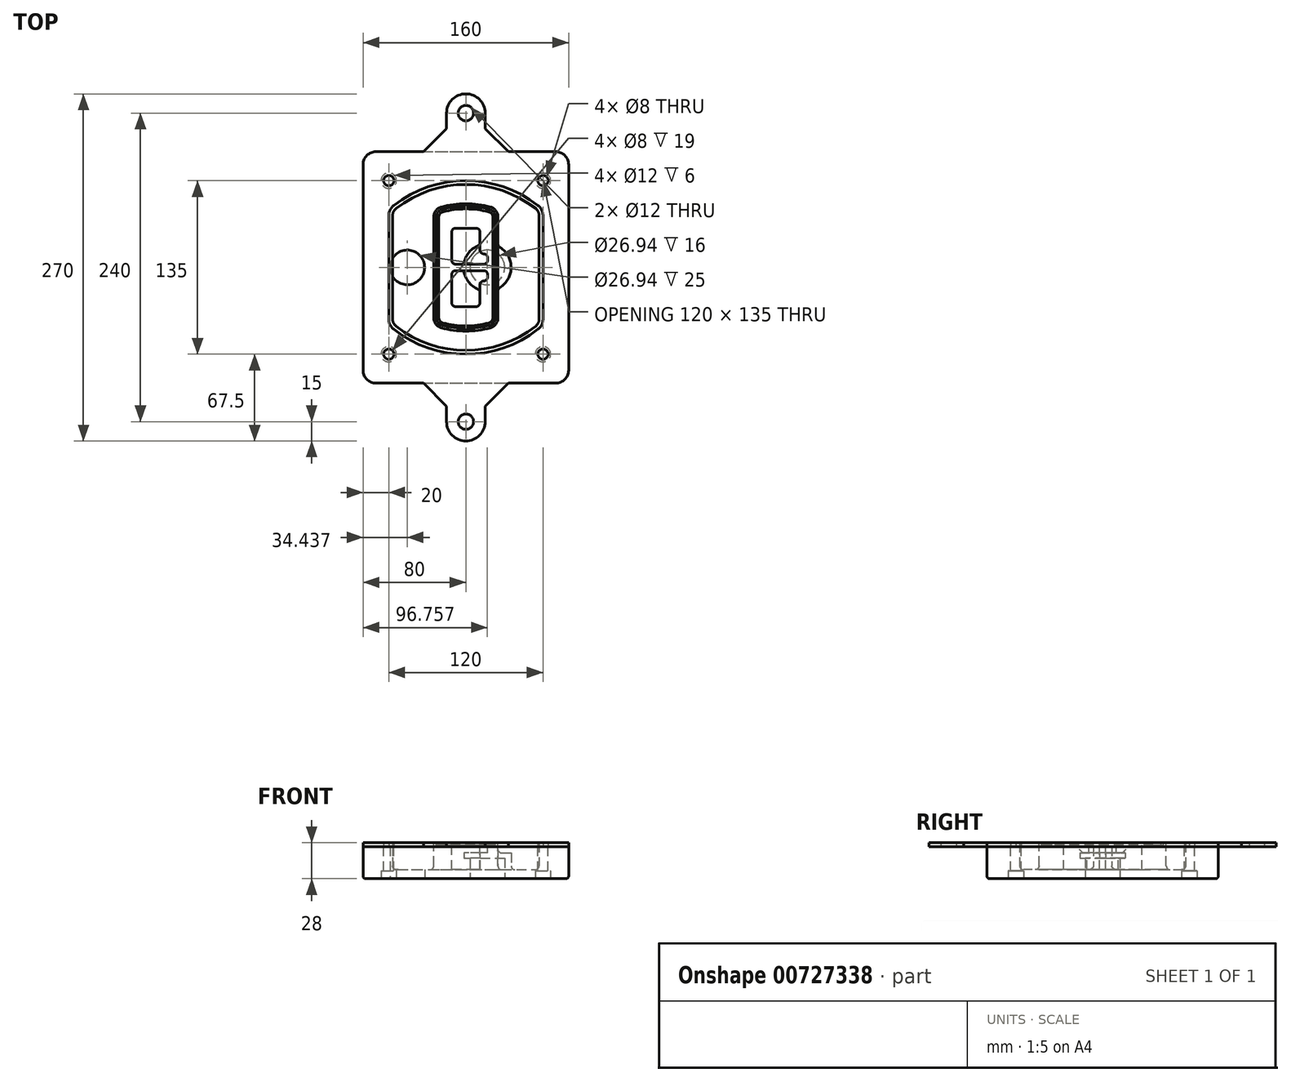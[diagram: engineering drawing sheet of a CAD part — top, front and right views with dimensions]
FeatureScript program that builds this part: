
annotation { "Feature Type Name" : "Feature", "Feature Type Description" : "" }
export const myFeature = defineFeature(function(context is Context, id is Id, definition is map)
    precondition{}
    {
        {
            var Q0;
            Q0=qCreatedBy(makeId("Top.planeOp"),FACE);
            var sketch = newSketch(context, id + "F0", { "sketchPlane" : qUnion([Q0])});
            skPoint(sketch, "E0.rect.middle", {"position": v(0, 0) * mm});
            skLineSegment(sketch, "E1.bottom", {"start": v(-70, -90) * mm, "end": v(70, -90) * mm});
            skLineSegment(sketch, "E1.top", {"start": v(-70, 90) * mm, "end": v(70, 90) * mm});
            skLineSegment(sketch, "E1.left", {"start": v(-80, -80) * mm, "end": v(-80, 80) * mm});
            skLineSegment(sketch, "E1.right", {"start": v(80, -80) * mm, "end": v(80, 80) * mm});
            skLineSegment(sketch, "E2", {"start": v(-80, 90) * mm, "end": v(80, -90) * mm, "construction": true});
            skLineSegment(sketch, "E3", {"start": v(80, 90) * mm, "end": v(-80, -90) * mm, "construction": true});
            skCircle(sketch, "E4", {"center": v(-60, 67.5) * mm, "radius": 4 * mm});
            skCircle(sketch, "E5", {"center": v(60, 67.5) * mm, "radius": 4 * mm});
            skCircle(sketch, "E6", {"center": v(60, -67.5) * mm, "radius": 4 * mm});
            skCircle(sketch, "E7", {"center": v(-60, -67.5) * mm, "radius": 4 * mm});
            skLineSegment(sketch, "E8", {"start": v(-60, 67.5) * mm, "end": v(60, 67.5) * mm, "construction": true});
            skLineSegment(sketch, "E9", {"start": v(60, 67.5) * mm, "end": v(60, -67.5) * mm, "construction": true});
            skLineSegment(sketch, "E10", {"start": v(60, -67.5) * mm, "end": v(-60, -67.5) * mm, "construction": true});
            skLineSegment(sketch, "E11", {"start": v(-60, -67.5) * mm, "end": v(-60, 67.5) * mm, "construction": true});
            skLineSegment(sketch, "E12", {"start": v(-60, 40.3) * mm, "end": v(-60, -40.3) * mm});
            skLineSegment(sketch, "E13", {"start": v(60, 40.3) * mm, "end": v(60, -40.3) * mm});
            skArc(sketch, "E14", {"start": v(56.15, 48.18) * mm, "mid": v(0, 67.5) * mm, "end": v(-56.15, 48.18) * mm});
            skArc(sketch, "E15", {"start": v(-56.15, -48.18) * mm, "mid": v(0, -67.5) * mm, "end": v(56.15, -48.18) * mm});
            skLineSegment(sketch, "E16", {"start": v(-60, 0) * mm, "end": v(60, 0) * mm, "construction": true});
            skPoint(sketch, "E17.visualSharp", {"position": v(-60, -45) * mm});
            skArc(sketch, "E17.filletArc", {"start": v(-60, -40.3) * mm, "mid": v(-58.99, -44.68) * mm, "end": v(-56.15, -48.18) * mm});
            skPoint(sketch, "E18.visualSharp", {"position": v(-60, 45) * mm});
            skArc(sketch, "E18.filletArc", {"start": v(-56.15, 48.18) * mm, "mid": v(-58.99, 44.68) * mm, "end": v(-60, 40.3) * mm});
            skPoint(sketch, "E19.visualSharp", {"position": v(60, 45) * mm});
            skArc(sketch, "E19.filletArc", {"start": v(60, 40.3) * mm, "mid": v(58.99, 44.68) * mm, "end": v(56.15, 48.18) * mm});
            skPoint(sketch, "E20.visualSharp", {"position": v(60, -45) * mm});
            skArc(sketch, "E20.filletArc", {"start": v(56.15, -48.18) * mm, "mid": v(58.99, -44.68) * mm, "end": v(60, -40.3) * mm});
            skPoint(sketch, "E21.visualSharp", {"position": v(-80, 90) * mm});
            skArc(sketch, "E21.filletArc", {"start": v(-70, 90) * mm, "mid": v(-77.07, 87.07) * mm, "end": v(-80, 80) * mm});
            skPoint(sketch, "E22.visualSharp", {"position": v(80, 90) * mm});
            skArc(sketch, "E22.filletArc", {"start": v(80, 80) * mm, "mid": v(77.07, 87.07) * mm, "end": v(70, 90) * mm});
            skPoint(sketch, "E23.visualSharp", {"position": v(80, -90) * mm});
            skArc(sketch, "E23.filletArc", {"start": v(70, -90) * mm, "mid": v(77.07, -87.07) * mm, "end": v(80, -80) * mm});
            skPoint(sketch, "E24.visualSharp", {"position": v(-80, -90) * mm});
            skArc(sketch, "E24.filletArc", {"start": v(-80, -80) * mm, "mid": v(-77.07, -87.07) * mm, "end": v(-70, -90) * mm});
            skArc(sketch, "E25.0", {"start": v(57, 40.3) * mm, "mid": v(56.3, 43.36) * mm, "end": v(54.3, 45.81) * mm});
            skLineSegment(sketch, "E25.1", {"start": v(57, 40.3) * mm, "end": v(57, -40.3) * mm});
            skArc(sketch, "E25.2", {"start": v(54.3, -45.81) * mm, "mid": v(56.3, -43.36) * mm, "end": v(57, -40.3) * mm});
            skArc(sketch, "E25.3", {"start": v(-54.3, -45.81) * mm, "mid": v(0, -64.5) * mm, "end": v(54.3, -45.81) * mm});
            skArc(sketch, "E25.4", {"start": v(-57, -40.3) * mm, "mid": v(-56.3, -43.36) * mm, "end": v(-54.3, -45.81) * mm});
            skArc(sketch, "E25.5", {"start": v(54.3, 45.81) * mm, "mid": v(0, 64.5) * mm, "end": v(-54.3, 45.81) * mm});
            skLineSegment(sketch, "E25.6", {"start": v(-57, 40.3) * mm, "end": v(-57, -40.3) * mm});
            skArc(sketch, "E25.7", {"start": v(-54.3, 45.81) * mm, "mid": v(-56.3, 43.36) * mm, "end": v(-57, 40.3) * mm});
            skArc(sketch, "E26.0", {"start": v(-58.62, 51.33) * mm, "mid": v(-62.58, 46.43) * mm, "end": v(-64, 40.3) * mm});
            skArc(sketch, "E26.1", {"start": v(58.62, 51.33) * mm, "mid": v(0, 71.5) * mm, "end": v(-58.62, 51.33) * mm});
            skArc(sketch, "E26.2", {"start": v(64, 40.3) * mm, "mid": v(62.58, 46.43) * mm, "end": v(58.62, 51.33) * mm});
            skLineSegment(sketch, "E26.3", {"start": v(64, 40.3) * mm, "end": v(64, -40.3) * mm});
            skArc(sketch, "E26.4", {"start": v(58.62, -51.33) * mm, "mid": v(62.58, -46.43) * mm, "end": v(64, -40.3) * mm});
            skLineSegment(sketch, "E26.5", {"start": v(-64, 40.3) * mm, "end": v(-64, -40.3) * mm});
            skArc(sketch, "E26.6", {"start": v(-58.62, -51.33) * mm, "mid": v(0, -71.5) * mm, "end": v(58.62, -51.33) * mm});
            skArc(sketch, "E26.7", {"start": v(-64, -40.3) * mm, "mid": v(-62.58, -46.43) * mm, "end": v(-58.62, -51.33) * mm});
            skSolve(sketch);
        }
        {
            var Q0;
            Q0=makeQuery(id+"F0.imprint","IMPRINT",FACE,{"disambiguationData":[TD([[makeQuery(id+"F0.imprint","IMPRINT",EDGE,{"derivedFrom":sQuery(id+"F0.wireOp",EDGE,"E1.bottom")}),1.0]])]});
            var Q1;
            Q1=makeQuery(id+"F0.imprint","IMPRINT",FACE,{"disambiguationData":[TD([[makeQuery(id+"F0.imprint","IMPRINT",EDGE,{"derivedFrom":sQuery(id+"F0.wireOp",EDGE,"E12")}),1.0]])]});
            var Q2;
            Q2=makeQuery(id+"F0.imprint","IMPRINT",FACE,{"disambiguationData":[TD([[makeQuery(id+"F0.imprint","IMPRINT",EDGE,{"derivedFrom":sQuery(id+"F0.wireOp",EDGE,"E25.0")}),1.0]])]});
            var Q3;
            Q3=makeQuery(id+"F0.imprint","IMPRINT",FACE,{"disambiguationData":[TD([[makeQuery(id+"F0.imprint","IMPRINT",EDGE,{"derivedFrom":sQuery(id+"F0.wireOp",EDGE,"E12")}),-1.0]])]});
            extrude(context, id + "F1", {"entities" : qUnion([Q0, Q1, Q2, Q3]), "oppositeDirection" : true, "depth" : 25 * mm});
        }
        {
            var Q0;
            Q0=makeQuery(id+"F0.imprint","IMPRINT",FACE,{"disambiguationData":[TD([[makeQuery(id+"F0.imprint","IMPRINT",EDGE,{"derivedFrom":sQuery(id+"F0.wireOp",EDGE,"E12")}),1.0]])]});
            extrude(context, id + "F2", {"entities" : qUnion([Q0]), "operationType" : NewBodyOperationType.ADD, "depth" : 3 * mm});
        }
        {
            var Q0;
            Q0=makeQuery(id+"F0.imprint","IMPRINT",FACE,{"disambiguationData":[TD([[makeQuery(id+"F0.imprint","IMPRINT",EDGE,{"derivedFrom":sQuery(id+"F0.wireOp",EDGE,"E25.0")}),1.0]])]});
            extrude(context, id + "F3", {"entities" : qUnion([Q0]), "operationType" : NewBodyOperationType.REMOVE, "oppositeDirection" : true, "depth" : 18 * mm});
        }
        {
            var Q0;
            Q0=makeQuery(id+"F2.opExtrude","CAP_FACE",FACE,{"disambiguationData":[OSD([sQuery(id+"F0.wireOp",EDGE,"E12"),sQuery(id+"F0.wireOp",EDGE,"E13"),sQuery(id+"F0.wireOp",EDGE,"E14"),sQuery(id+"F0.wireOp",EDGE,"E15"),sQuery(id+"F0.wireOp",EDGE,"E17.filletArc"),sQuery(id+"F0.wireOp",EDGE,"E18.filletArc"),sQuery(id+"F0.wireOp",EDGE,"E19.filletArc"),sQuery(id+"F0.wireOp",EDGE,"E20.filletArc"),sQuery(id+"F0.wireOp",EDGE,"E25.0"),sQuery(id+"F0.wireOp",EDGE,"E25.1"),sQuery(id+"F0.wireOp",EDGE,"E25.2"),sQuery(id+"F0.wireOp",EDGE,"E25.3"),sQuery(id+"F0.wireOp",EDGE,"E25.4"),sQuery(id+"F0.wireOp",EDGE,"E25.5"),sQuery(id+"F0.wireOp",EDGE,"E25.6"),sQuery(id+"F0.wireOp",EDGE,"E25.7")])],"isStart":false});
            var sketch = newSketch(context, id + "F4", { "sketchPlane" : qUnion([Q0])});
            skArc(sketch, "E27.0", {"start": v(-19.08, -46.97) * mm, "mid": v(0, -49.5) * mm, "end": v(19.08, -46.97) * mm});
            skArc(sketch, "E28.0", {"start": v(19.08, 46.97) * mm, "mid": v(0, 49.5) * mm, "end": v(-19.08, 46.97) * mm});
            skLineSegment(sketch, "E29", {"start": v(-25, 39.25) * mm, "end": v(-25, -39.25) * mm});
            skLineSegment(sketch, "E30", {"start": v(25, 39.25) * mm, "end": v(25, -39.25) * mm});
            skLineSegment(sketch, "E31", {"start": v(-25, 45.1) * mm, "end": v(25, 45.1) * mm, "construction": true});
            skLineSegment(sketch, "E32", {"start": v(-25, -45.1) * mm, "end": v(25, -45.1) * mm, "construction": true});
            skPoint(sketch, "E33.visualSharp", {"position": v(-25, 45.1) * mm});
            skArc(sketch, "E33.filletArc", {"start": v(-19.08, 46.97) * mm, "mid": v(-23.35, 44.11) * mm, "end": v(-25, 39.25) * mm});
            skPoint(sketch, "E34.visualSharp", {"position": v(25, 45.1) * mm});
            skArc(sketch, "E34.filletArc", {"start": v(25, 39.25) * mm, "mid": v(23.35, 44.11) * mm, "end": v(19.08, 46.97) * mm});
            skPoint(sketch, "E35.visualSharp", {"position": v(25, -45.1) * mm});
            skArc(sketch, "E35.filletArc", {"start": v(19.08, -46.97) * mm, "mid": v(23.35, -44.11) * mm, "end": v(25, -39.25) * mm});
            skPoint(sketch, "E36.visualSharp", {"position": v(-25, -45.1) * mm});
            skArc(sketch, "E36.filletArc", {"start": v(-25, -39.25) * mm, "mid": v(-23.35, -44.11) * mm, "end": v(-19.08, -46.97) * mm});
            skArc(sketch, "E37.0", {"start": v(54.3, 45.81) * mm, "mid": v(0, 64.5) * mm, "end": v(-54.3, 45.81) * mm});
            skArc(sketch, "E37.1", {"start": v(-54.3, 45.81) * mm, "mid": v(-56.3, 43.36) * mm, "end": v(-57, 40.3) * mm});
            skLineSegment(sketch, "E37.2", {"start": v(-57, 40.3) * mm, "end": v(-57, -40.3) * mm});
            skArc(sketch, "E37.3", {"start": v(-57, -40.3) * mm, "mid": v(-56.3, -43.36) * mm, "end": v(-54.3, -45.81) * mm});
            skArc(sketch, "E37.4", {"start": v(-54.3, -45.81) * mm, "mid": v(0, -64.5) * mm, "end": v(54.3, -45.81) * mm});
            skArc(sketch, "E37.5", {"start": v(54.3, -45.81) * mm, "mid": v(56.3, -43.36) * mm, "end": v(57, -40.3) * mm});
            skLineSegment(sketch, "E37.6", {"start": v(57, 40.3) * mm, "end": v(57, -40.3) * mm});
            skArc(sketch, "E37.7", {"start": v(57, 40.3) * mm, "mid": v(56.3, 43.36) * mm, "end": v(54.3, 45.81) * mm});
            skLineSegment(sketch, "E38.0", {"start": v(23, 39.25) * mm, "end": v(23, -39.25) * mm});
            skArc(sketch, "E38.1", {"start": v(18.56, -45.04) * mm, "mid": v(21.76, -42.9) * mm, "end": v(23, -39.25) * mm});
            skArc(sketch, "E38.2", {"start": v(-18.56, -45.04) * mm, "mid": v(0, -47.5) * mm, "end": v(18.56, -45.04) * mm});
            skArc(sketch, "E38.3", {"start": v(-23, -39.25) * mm, "mid": v(-21.76, -42.9) * mm, "end": v(-18.56, -45.04) * mm});
            skLineSegment(sketch, "E38.4", {"start": v(-23, 39.25) * mm, "end": v(-23, -39.25) * mm});
            skArc(sketch, "E38.5", {"start": v(23, 39.25) * mm, "mid": v(21.76, 42.9) * mm, "end": v(18.56, 45.04) * mm});
            skArc(sketch, "E38.6", {"start": v(-18.56, 45.04) * mm, "mid": v(-21.76, 42.9) * mm, "end": v(-23, 39.25) * mm});
            skArc(sketch, "E38.7", {"start": v(18.56, 45.04) * mm, "mid": v(0, 47.5) * mm, "end": v(-18.56, 45.04) * mm});
            skArc(sketch, "E39.0", {"start": v(21, 39.25) * mm, "mid": v(20.18, 41.68) * mm, "end": v(18.04, 43.1) * mm});
            skLineSegment(sketch, "E39.1", {"start": v(21, 39.25) * mm, "end": v(21, -39.25) * mm});
            skArc(sketch, "E39.2", {"start": v(18.04, -43.1) * mm, "mid": v(20.18, -41.68) * mm, "end": v(21, -39.25) * mm});
            skArc(sketch, "E39.3", {"start": v(-18.04, -43.1) * mm, "mid": v(0, -45.5) * mm, "end": v(18.04, -43.1) * mm});
            skArc(sketch, "E39.4", {"start": v(-21, -39.25) * mm, "mid": v(-20.18, -41.68) * mm, "end": v(-18.04, -43.1) * mm});
            skArc(sketch, "E39.5", {"start": v(18.04, 43.1) * mm, "mid": v(0, 45.5) * mm, "end": v(-18.04, 43.1) * mm});
            skLineSegment(sketch, "E39.6", {"start": v(-21, 39.25) * mm, "end": v(-21, -39.25) * mm});
            skArc(sketch, "E39.7", {"start": v(-18.04, 43.1) * mm, "mid": v(-20.18, 41.68) * mm, "end": v(-21, 39.25) * mm});
            skLineSegment(sketch, "E40", {"start": v(-25, 0) * mm, "end": v(25, 0) * mm, "construction": true});
            skLineSegment(sketch, "E41", {"start": v(-11, 5.5) * mm, "end": v(-11, 27.5) * mm});
            skLineSegment(sketch, "E42", {"start": v(-8, 30.5) * mm, "end": v(8, 30.5) * mm});
            skLineSegment(sketch, "E43", {"start": v(11, 27.5) * mm, "end": v(11, 13.5) * mm});
            skLineSegment(sketch, "E44", {"start": v(14, 10.5) * mm, "end": v(14, 10.5) * mm});
            skLineSegment(sketch, "E45", {"start": v(17, 7.5) * mm, "end": v(17, 5.5) * mm});
            skLineSegment(sketch, "E46", {"start": v(14, 2.5) * mm, "end": v(-8, 2.5) * mm});
            skPoint(sketch, "E47.visualSharp", {"position": v(-11, 30.5) * mm});
            skArc(sketch, "E47.filletArc", {"start": v(-8, 30.5) * mm, "mid": v(-10.12, 29.62) * mm, "end": v(-11, 27.5) * mm});
            skPoint(sketch, "E48.visualSharp", {"position": v(11, 30.5) * mm});
            skArc(sketch, "E48.filletArc", {"start": v(11, 27.5) * mm, "mid": v(10.12, 29.62) * mm, "end": v(8, 30.5) * mm});
            skPoint(sketch, "E49.visualSharp", {"position": v(11, 10.5) * mm});
            skArc(sketch, "E49.filletArc", {"start": v(11, 13.5) * mm, "mid": v(11.88, 11.38) * mm, "end": v(14, 10.5) * mm});
            skPoint(sketch, "E50.visualSharp", {"position": v(17, 10.5) * mm});
            skArc(sketch, "E50.filletArc", {"start": v(17, 7.5) * mm, "mid": v(16.12, 9.62) * mm, "end": v(14, 10.5) * mm});
            skPoint(sketch, "E51.visualSharp", {"position": v(17, 2.5) * mm});
            skArc(sketch, "E51.filletArc", {"start": v(14, 2.5) * mm, "mid": v(16.12, 3.38) * mm, "end": v(17, 5.5) * mm});
            skPoint(sketch, "E52.visualSharp", {"position": v(-11, 2.5) * mm});
            skArc(sketch, "E52.filletArc", {"start": v(-11, 5.5) * mm, "mid": v(-10.12, 3.38) * mm, "end": v(-8, 2.5) * mm});
            skLineSegment(sketch, "E53.0.MirrorCS", {"start": v(14, -2.5) * mm, "end": v(-8, -2.5) * mm});
            skArc(sketch, "E54.0.MirrorCS", {"start": v(-11, -5.5) * mm, "mid": v(-10.12, -3.38) * mm, "end": v(-8, -2.5) * mm});
            skLineSegment(sketch, "E55.0.MirrorCS", {"start": v(-11, -5.5) * mm, "end": v(-11, -27.5) * mm});
            skArc(sketch, "E56.0.MirrorCS", {"start": v(-8, -30.5) * mm, "mid": v(-10.12, -29.62) * mm, "end": v(-11, -27.5) * mm});
            skLineSegment(sketch, "E57.0.MirrorCS", {"start": v(-8, -30.5) * mm, "end": v(8, -30.5) * mm});
            skArc(sketch, "E58.0.MirrorCS", {"start": v(11, -27.5) * mm, "mid": v(10.12, -29.62) * mm, "end": v(8, -30.5) * mm});
            skLineSegment(sketch, "E59.0.MirrorCS", {"start": v(11, -27.5) * mm, "end": v(11, -13.5) * mm});
            skArc(sketch, "E60.0.MirrorCS", {"start": v(11, -13.5) * mm, "mid": v(11.88, -11.38) * mm, "end": v(14, -10.5) * mm});
            skArc(sketch, "E61.0.MirrorCS", {"start": v(17, -7.5) * mm, "mid": v(16.12, -9.62) * mm, "end": v(14, -10.5) * mm});
            skLineSegment(sketch, "E62.0.MirrorCS", {"start": v(17, -7.5) * mm, "end": v(17, -5.5) * mm});
            skArc(sketch, "E63.0.MirrorCS", {"start": v(14, -2.5) * mm, "mid": v(16.12, -3.38) * mm, "end": v(17, -5.5) * mm});
            skSolve(sketch);
        }
        {
            var Q0;
            Q0=makeQuery(id+"F4.imprint","IMPRINT",FACE,{"disambiguationData":[TD([[makeQuery(id+"F4.imprint","IMPRINT",EDGE,{"derivedFrom":sQuery(id+"F4.wireOp",EDGE,"E27.0")}),1.0]])]});
            var Q1;
            Q1=makeQuery(id+"F4.imprint","IMPRINT",FACE,{"disambiguationData":[TD([[makeQuery(id+"F4.imprint","IMPRINT",EDGE,{"derivedFrom":sQuery(id+"F4.wireOp",EDGE,"E38.0")}),-1.0]])]});
            var Q2;
            Q2=makeQuery(id+"F4.imprint","IMPRINT",FACE,{"disambiguationData":[TD([[makeQuery(id+"F4.imprint","IMPRINT",EDGE,{"derivedFrom":sQuery(id+"F4.wireOp",EDGE,"E39.0")}),1.0]])]});
            extrude(context, id + "F5", {"entities" : qUnion([Q0, Q1, Q2]), "operationType" : NewBodyOperationType.ADD, "endBound" : BoundingType.UP_TO_NEXT, "oppositeDirection" : true, "depth" : 25 * mm});
        }
        {
            var Q0;
            Q0=makeQuery(id+"F4.imprint","IMPRINT",FACE,{"disambiguationData":[TD([[makeQuery(id+"F4.imprint","IMPRINT",EDGE,{"derivedFrom":sQuery(id+"F4.wireOp",EDGE,"E38.0")}),-1.0]])]});
            extrude(context, id + "F6", {"entities" : qUnion([Q0]), "operationType" : NewBodyOperationType.REMOVE, "oppositeDirection" : true, "depth" : 2 * mm});
        }
        {
            var Q0;
            Q0=makeQuery(id+"F1.opExtrude","CAP_FACE",FACE,{"disambiguationData":[OSD([sQuery(id+"F0.wireOp",EDGE,"E1.bottom"),sQuery(id+"F0.wireOp",EDGE,"E1.top"),sQuery(id+"F0.wireOp",EDGE,"E1.left"),sQuery(id+"F0.wireOp",EDGE,"E1.right"),sQuery(id+"F0.wireOp",EDGE,"E4"),sQuery(id+"F0.wireOp",EDGE,"E5"),sQuery(id+"F0.wireOp",EDGE,"E6"),sQuery(id+"F0.wireOp",EDGE,"E7"),sQuery(id+"F0.wireOp",EDGE,"E21.filletArc"),sQuery(id+"F0.wireOp",EDGE,"E22.filletArc"),sQuery(id+"F0.wireOp",EDGE,"E23.filletArc"),sQuery(id+"F0.wireOp",EDGE,"E24.filletArc")])],"isStart":false});
            var sketch = newSketch(context, id + "F7", { "sketchPlane" : qUnion([Q0])});
            skCircle(sketch, "E64", {"center": v(16.76, 0) * mm, "radius": 13.47 * mm});
            skCircle(sketch, "E65", {"center": v(-45.56, 0) * mm, "radius": 13.47 * mm});
            skLineSegment(sketch, "E66", {"start": v(80, 0) * mm, "end": v(-80, 0) * mm});
            skCircle(sketch, "E67", {"center": v(16.76, 0) * mm, "radius": 18.47 * mm});
            skCircle(sketch, "E68", {"center": v(60, -67.5) * mm, "radius": 6 * mm});
            skCircle(sketch, "E69", {"center": v(-60, -67.5) * mm, "radius": 6 * mm});
            skCircle(sketch, "E70", {"center": v(-60, 67.5) * mm, "radius": 6 * mm});
            skCircle(sketch, "E71", {"center": v(60, 67.5) * mm, "radius": 6 * mm});
            skSolve(sketch);
        }
        {
            var Q0;
            {var subQ1=sQuery(id+"F7.wireOp",EDGE,"E66");var subQ4=sQuery(id+"F7.wireOp",EDGE,"E64");var subQ6=makeQuery(id+"F7.imprint","INTERSECT",VERTEX,{"disambiguationData":[OD(0.0)],"derivedFrom":[subQ4,subQ1]});Q0=makeQuery(id+"F7.imprint","IMPRINT",FACE,{"disambiguationData":[TD([[makeQuery(id+"F7.imprint","IMPRINT",EDGE,{"disambiguationData":[TD([[subQ6,-1.0]])],"derivedFrom":subQ4}),-1.0]])]});}
            var Q1;
            {var subQ0=sQuery(id+"F7.wireOp",EDGE,"E66");var subQ1=sQuery(id+"F7.wireOp",EDGE,"E64");var subQ3=makeQuery(id+"F7.imprint","INTERSECT",VERTEX,{"disambiguationData":[OD(0.0)],"derivedFrom":[subQ1,subQ0]});Q1=makeQuery(id+"F7.imprint","IMPRINT",FACE,{"disambiguationData":[TD([[makeQuery(id+"F7.imprint","IMPRINT",EDGE,{"disambiguationData":[TD([[subQ3,-1.0]])],"derivedFrom":subQ1}),1.0]])]});}
            var Q2;
            {var subQ0=sQuery(id+"F7.wireOp",EDGE,"E66");var subQ1=sQuery(id+"F7.wireOp",EDGE,"E64");var subQ3=makeQuery(id+"F7.imprint","INTERSECT",VERTEX,{"disambiguationData":[OD(0.0)],"derivedFrom":[subQ1,subQ0]});Q2=makeQuery(id+"F7.imprint","IMPRINT",FACE,{"disambiguationData":[TD([[makeQuery(id+"F7.imprint","IMPRINT",EDGE,{"disambiguationData":[TD([[subQ3,1.0]])],"derivedFrom":subQ1}),1.0]])]});}
            var Q3;
            {var subQ1=sQuery(id+"F7.wireOp",EDGE,"E66");var subQ4=sQuery(id+"F7.wireOp",EDGE,"E64");var subQ6=makeQuery(id+"F7.imprint","INTERSECT",VERTEX,{"disambiguationData":[OD(0.0)],"derivedFrom":[subQ4,subQ1]});Q3=makeQuery(id+"F7.imprint","IMPRINT",FACE,{"disambiguationData":[TD([[makeQuery(id+"F7.imprint","IMPRINT",EDGE,{"disambiguationData":[TD([[subQ6,1.0]])],"derivedFrom":subQ4}),-1.0]])]});}
            extrude(context, id + "F8", {"entities" : qUnion([Q0, Q1, Q2, Q3]), "operationType" : NewBodyOperationType.ADD, "oppositeDirection" : true, "depth" : 20 * mm});
        }
        {
            var Q0;
            {var subQ0=sQuery(id+"F7.wireOp",EDGE,"E66");var subQ1=sQuery(id+"F7.wireOp",EDGE,"E64");var subQ3=makeQuery(id+"F7.imprint","INTERSECT",VERTEX,{"disambiguationData":[OD(0.0)],"derivedFrom":[subQ1,subQ0]});Q0=makeQuery(id+"F7.imprint","IMPRINT",FACE,{"disambiguationData":[TD([[makeQuery(id+"F7.imprint","IMPRINT",EDGE,{"disambiguationData":[TD([[subQ3,-1.0]])],"derivedFrom":subQ1}),1.0]])]});}
            var Q1;
            {var subQ0=sQuery(id+"F7.wireOp",EDGE,"E66");var subQ1=sQuery(id+"F7.wireOp",EDGE,"E64");var subQ3=makeQuery(id+"F7.imprint","INTERSECT",VERTEX,{"disambiguationData":[OD(0.0)],"derivedFrom":[subQ1,subQ0]});Q1=makeQuery(id+"F7.imprint","IMPRINT",FACE,{"disambiguationData":[TD([[makeQuery(id+"F7.imprint","IMPRINT",EDGE,{"disambiguationData":[TD([[subQ3,1.0]])],"derivedFrom":subQ1}),1.0]])]});}
            extrude(context, id + "F9", {"entities" : qUnion([Q0, Q1]), "operationType" : NewBodyOperationType.REMOVE, "oppositeDirection" : true, "depth" : 16 * mm});
        }
        {
            var Q0;
            {var subQ0=sQuery(id+"F7.wireOp",EDGE,"E66");var subQ1=sQuery(id+"F7.wireOp",EDGE,"E65");var subQ3=makeQuery(id+"F7.imprint","INTERSECT",VERTEX,{"disambiguationData":[OD(0.0)],"derivedFrom":[subQ1,subQ0]});Q0=makeQuery(id+"F7.imprint","IMPRINT",FACE,{"disambiguationData":[TD([[makeQuery(id+"F7.imprint","IMPRINT",EDGE,{"disambiguationData":[TD([[subQ3,-1.0]])],"derivedFrom":subQ1}),1.0]])]});}
            var Q1;
            {var subQ0=sQuery(id+"F7.wireOp",EDGE,"E66");var subQ1=sQuery(id+"F7.wireOp",EDGE,"E65");var subQ3=makeQuery(id+"F7.imprint","INTERSECT",VERTEX,{"disambiguationData":[OD(0.0)],"derivedFrom":[subQ1,subQ0]});Q1=makeQuery(id+"F7.imprint","IMPRINT",FACE,{"disambiguationData":[TD([[makeQuery(id+"F7.imprint","IMPRINT",EDGE,{"disambiguationData":[TD([[subQ3,1.0]])],"derivedFrom":subQ1}),1.0]])]});}
            extrude(context, id + "F10", {"entities" : qUnion([Q0, Q1]), "operationType" : NewBodyOperationType.REMOVE, "oppositeDirection" : true, "depth" : 25 * mm});
        }
        {
            var Q0;
            Q0=makeQuery(id+"F7.imprint","IMPRINT",FACE,{"disambiguationData":[TD([[makeQuery(id+"F7.imprint","IMPRINT",EDGE,{"derivedFrom":sQuery(id+"F7.wireOp",EDGE,"E68")}),1.0]])]});
            var Q1;
            Q1=makeQuery(id+"F7.imprint","IMPRINT",FACE,{"disambiguationData":[TD([[makeQuery(id+"F7.imprint","IMPRINT",EDGE,{"derivedFrom":makeQuery(id+"F1.opExtrude","CAP_EDGE",EDGE,{"disambiguationData":[OSD([sQuery(id+"F0.wireOp",EDGE,"E5")])],"isStart":false})}),-1.0]])]});
            var Q2;
            Q2=makeQuery(id+"F7.imprint","IMPRINT",FACE,{"disambiguationData":[TD([[makeQuery(id+"F7.imprint","IMPRINT",EDGE,{"derivedFrom":sQuery(id+"F7.wireOp",EDGE,"E69")}),1.0]])]});
            var Q3;
            Q3=makeQuery(id+"F7.imprint","IMPRINT",FACE,{"disambiguationData":[TD([[makeQuery(id+"F7.imprint","IMPRINT",EDGE,{"derivedFrom":makeQuery(id+"F1.opExtrude","CAP_EDGE",EDGE,{"disambiguationData":[OSD([sQuery(id+"F0.wireOp",EDGE,"E4")])],"isStart":false})}),-1.0]])]});
            var Q4;
            Q4=makeQuery(id+"F7.imprint","IMPRINT",FACE,{"disambiguationData":[TD([[makeQuery(id+"F7.imprint","IMPRINT",EDGE,{"derivedFrom":sQuery(id+"F7.wireOp",EDGE,"E70")}),1.0]])]});
            var Q5;
            Q5=makeQuery(id+"F7.imprint","IMPRINT",FACE,{"disambiguationData":[TD([[makeQuery(id+"F7.imprint","IMPRINT",EDGE,{"derivedFrom":makeQuery(id+"F1.opExtrude","CAP_EDGE",EDGE,{"disambiguationData":[OSD([sQuery(id+"F0.wireOp",EDGE,"E7")])],"isStart":false})}),-1.0]])]});
            var Q6;
            Q6=makeQuery(id+"F7.imprint","IMPRINT",FACE,{"disambiguationData":[TD([[makeQuery(id+"F7.imprint","IMPRINT",EDGE,{"derivedFrom":sQuery(id+"F7.wireOp",EDGE,"E71")}),1.0]])]});
            var Q7;
            Q7=makeQuery(id+"F7.imprint","IMPRINT",FACE,{"disambiguationData":[TD([[makeQuery(id+"F7.imprint","IMPRINT",EDGE,{"derivedFrom":makeQuery(id+"F1.opExtrude","CAP_EDGE",EDGE,{"disambiguationData":[OSD([sQuery(id+"F0.wireOp",EDGE,"E6")])],"isStart":false})}),-1.0]])]});
            extrude(context, id + "F11", {"entities" : qUnion([Q0, Q1, Q2, Q3, Q4, Q5, Q6, Q7]), "operationType" : NewBodyOperationType.REMOVE, "oppositeDirection" : true, "depth" : 6 * mm});
        }
        {
            var Q0;
            Q0=makeQuery(id+"F9.boolean.opBoolean","COPY",FACE,{"derivedFrom":makeQuery(id+"F9.opExtrude","CAP_FACE",FACE,{"disambiguationData":[OSD([sQuery(id+"F7.wireOp",EDGE,"E64")])],"isStart":false})});
            var sketch = newSketch(context, id + "F12", { "sketchPlane" : qUnion([Q0])});
            skArc(sketch, "E72.0", {"start": v(11, 17.55) * mm, "mid": v(2.57, 11.82) * mm, "end": v(-1.54, 2.5) * mm});
            skArc(sketch, "E72.1", {"start": v(-1.54, -2.5) * mm, "mid": v(2.57, -11.82) * mm, "end": v(11, -17.55) * mm});
            skLineSegment(sketch, "E73", {"start": v(-1.54, -2.5) * mm, "end": v(14, -2.5) * mm});
            skLineSegment(sketch, "E74.0", {"start": v(14, 2.5) * mm, "end": v(-1.54, 2.5) * mm});
            skArc(sketch, "E74.1", {"start": v(14, 2.5) * mm, "mid": v(16.12, 3.38) * mm, "end": v(17, 5.5) * mm});
            skLineSegment(sketch, "E74.2", {"start": v(17, 7.5) * mm, "end": v(17, 5.5) * mm});
            skArc(sketch, "E74.3", {"start": v(17, 7.5) * mm, "mid": v(16.12, 9.62) * mm, "end": v(14, 10.5) * mm});
            skArc(sketch, "E74.4", {"start": v(11, 13.5) * mm, "mid": v(11.88, 11.38) * mm, "end": v(14, 10.5) * mm});
            skLineSegment(sketch, "E74.5", {"start": v(11, 17.55) * mm, "end": v(11, 13.5) * mm});
            skLineSegment(sketch, "E74.7", {"start": v(14, -2.5) * mm, "end": v(-1.54, -2.5) * mm});
            skArc(sketch, "E74.8", {"start": v(14, -2.5) * mm, "mid": v(16.12, -3.38) * mm, "end": v(17, -5.5) * mm});
            skLineSegment(sketch, "E74.9", {"start": v(17, -7.5) * mm, "end": v(17, -5.5) * mm});
            skArc(sketch, "E74.10", {"start": v(17, -7.5) * mm, "mid": v(16.12, -9.62) * mm, "end": v(14, -10.5) * mm});
            skArc(sketch, "E74.11", {"start": v(11, -13.5) * mm, "mid": v(11.88, -11.38) * mm, "end": v(14, -10.5) * mm});
            skLineSegment(sketch, "E74.12", {"start": v(11, -17.55) * mm, "end": v(11, -13.5) * mm});
            skPoint(sketch, "E75.orphan", {"position": v(11, -27.5) * mm});
            skPoint(sketch, "E76.orphan", {"position": v(-8, -2.5) * mm});
            skPoint(sketch, "E77.orphan", {"position": v(-8, 2.5) * mm});
            skPoint(sketch, "E78.orphan", {"position": v(11, 27.5) * mm});
            skSolve(sketch);
        }
        {
            var Q0;
            {var subQ7=sQuery(id+"F12.wireOp",EDGE,"E72.0");var subQ14=sQuery(id+"F12.wireOp",EDGE,"E72.1");var subQ16=sQuery(id+"F12.wireOp",EDGE,"E74.1");var subQ18=sQuery(id+"F12.wireOp",EDGE,"E74.8");Q0=qUnion([makeQuery(id+"F12.imprint","IMPRINT",FACE,{"disambiguationData":[TD([[makeQuery(id+"F12.imprint","IMPRINT",EDGE,{"derivedFrom":subQ7}),1.0]])]}),makeQuery(id+"F12.imprint","IMPRINT",FACE,{"disambiguationData":[TD([[makeQuery(id+"F12.imprint","IMPRINT",EDGE,{"derivedFrom":subQ14}),1.0]])]}),makeQuery(id+"F12.imprint","IMPRINT",FACE,{"disambiguationData":[TD([[makeQuery(id+"F12.imprint","IMPRINT",EDGE,{"derivedFrom":subQ16}),1.0]])]}),makeQuery(id+"F12.imprint","IMPRINT",FACE,{"disambiguationData":[TD([[makeQuery(id+"F12.imprint","IMPRINT",EDGE,{"derivedFrom":subQ18}),-1.0]])]})]);}
            var Q1;
            Q1=makeQuery(id+"F5.boolean.opBoolean","SPLIT",FACE,{"disambiguationData":[TD([makeQuery(id+"F5.opExtrude","SWEPT_FACE",FACE,{"disambiguationData":[OSD([sQuery(id+"F4.wireOp",EDGE,"E41")])]})])],"derivedFrom":makeQuery(id+"F3.boolean.opBoolean","COPY",FACE,{"derivedFrom":makeQuery(id+"F3.opExtrude","CAP_FACE",FACE,{"disambiguationData":[OSD([sQuery(id+"F0.wireOp",EDGE,"E25.0"),sQuery(id+"F0.wireOp",EDGE,"E25.1"),sQuery(id+"F0.wireOp",EDGE,"E25.2"),sQuery(id+"F0.wireOp",EDGE,"E25.3"),sQuery(id+"F0.wireOp",EDGE,"E25.4"),sQuery(id+"F0.wireOp",EDGE,"E25.5"),sQuery(id+"F0.wireOp",EDGE,"E25.6"),sQuery(id+"F0.wireOp",EDGE,"E25.7")])],"isStart":false})})});
            extrude(context, id + "F13", {"entities" : qUnion([Q0]), "operationType" : NewBodyOperationType.REMOVE, "endBound" : BoundingType.UP_TO_SURFACE, "endBoundEntityFace" : qUnion([Q1]), "depth" : 25 * mm});
        }
        {
            var Q0;
            Q0=makeQuery(id+"F3.boolean.opBoolean","COPY",EDGE,{"derivedFrom":makeQuery(id+"F3.opExtrude","CAP_EDGE",EDGE,{"disambiguationData":[OSD([sQuery(id+"F0.wireOp",EDGE,"E25.6")])],"isStart":false})});
            var Q1;
            Q1=makeQuery(id+"F8.boolean.opBoolean","INTERSECT",EDGE,{"derivedFrom":[makeQuery(id+"F5.opExtrude","SWEPT_FACE",FACE,{"disambiguationData":[OSD([sQuery(id+"F4.wireOp",EDGE,"E30")])]}),makeQuery(id+"F8.opExtrude","CAP_FACE",FACE,{"disambiguationData":[OSD([sQuery(id+"F7.wireOp",EDGE,"E67")])],"isStart":false})]});
            var Q2;
            Q2=makeQuery(id+"F8.boolean.opBoolean","INTERSECT",EDGE,{"disambiguationData":[OD(1.0)],"derivedFrom":[makeQuery(id+"F5.opExtrude","SWEPT_FACE",FACE,{"disambiguationData":[OSD([sQuery(id+"F4.wireOp",EDGE,"E30")])]}),makeQuery(id+"F8.opExtrude","SWEPT_FACE",FACE,{"disambiguationData":[OSD([sQuery(id+"F7.wireOp",EDGE,"E67")])]})]});
            var Q3;
            {var subQ0=sQuery(id+"F4.wireOp",EDGE,"E30");Q3=makeQuery(id+"F8.boolean.opBoolean","SPLIT",EDGE,{"disambiguationData":[TD([makeQuery(id+"F5.opExtrude","SWEPT_FACE",FACE,{"disambiguationData":[OSD([sQuery(id+"F4.wireOp",EDGE,"E35.filletArc")])]})])],"derivedFrom":makeQuery(id+"F5.opExtrude","CAP_EDGE",EDGE,{"disambiguationData":[OSD([subQ0])],"isStart":false})});}
            var Q4;
            {var subQ0=sQuery(id+"F0.wireOp",EDGE,"E25.7");var subQ1=sQuery(id+"F0.wireOp",EDGE,"E25.1");var subQ2=sQuery(id+"F0.wireOp",EDGE,"E25.6");var subQ3=sQuery(id+"F0.wireOp",EDGE,"E25.5");var subQ4=sQuery(id+"F0.wireOp",EDGE,"E25.4");var subQ5=sQuery(id+"F0.wireOp",EDGE,"E25.0");var subQ6=sQuery(id+"F0.wireOp",EDGE,"E25.2");var subQ7=sQuery(id+"F0.wireOp",EDGE,"E25.3");Q4=makeQuery(id+"F8.boolean.opBoolean","INTERSECT",EDGE,{"derivedFrom":[makeQuery(id+"F5.boolean.opBoolean","SPLIT",FACE,{"disambiguationData":[TD([makeQuery(id+"F2.opExtrude","SWEPT_FACE",FACE,{"disambiguationData":[OSD([subQ5])]})])],"derivedFrom":makeQuery(id+"F3.boolean.opBoolean","COPY",FACE,{"derivedFrom":makeQuery(id+"F3.opExtrude","CAP_FACE",FACE,{"disambiguationData":[OSD([subQ5,subQ1,subQ6,subQ7,subQ4,subQ3,subQ2,subQ0])],"isStart":false})})}),makeQuery(id+"F8.opExtrude","SWEPT_FACE",FACE,{"disambiguationData":[OSD([sQuery(id+"F7.wireOp",EDGE,"E67")])]})]});}
            var Q5;
            Q5=makeQuery(id+"F8.boolean.opBoolean","INTERSECT",EDGE,{"disambiguationData":[OD(0.0)],"derivedFrom":[makeQuery(id+"F5.opExtrude","SWEPT_FACE",FACE,{"disambiguationData":[OSD([sQuery(id+"F4.wireOp",EDGE,"E30")])]}),makeQuery(id+"F8.opExtrude","SWEPT_FACE",FACE,{"disambiguationData":[OSD([sQuery(id+"F7.wireOp",EDGE,"E67")])]})]});
            fillet(context, id + "F14", {"entities" : qUnion([Q0, Q1, Q2, Q3, Q4, Q5]), "radius" : 3 * mm, "tangentPropagation" : true, "allowEdgeOverflow" : false});
        }
        {
            var Q0;
            Q0=makeQuery(id+"F1.opExtrude","CAP_EDGE",EDGE,{"disambiguationData":[OSD([sQuery(id+"F0.wireOp",EDGE,"E1.bottom")])],"isStart":false});
            fillet(context, id + "F15", {"entities" : qUnion([Q0]), "radius" : 2 * mm, "tangentPropagation" : true, "allowEdgeOverflow" : false});
        }
        {
            var Q0;
            {var subQ0=sQuery(id+"F0.wireOp",EDGE,"E21.filletArc");var subQ1=sQuery(id+"F0.wireOp",EDGE,"E7");var subQ2=sQuery(id+"F0.wireOp",EDGE,"E6");var subQ3=sQuery(id+"F0.wireOp",EDGE,"E5");var subQ4=sQuery(id+"F0.wireOp",EDGE,"E4");var subQ5=sQuery(id+"F0.wireOp",EDGE,"E22.filletArc");var subQ6=sQuery(id+"F0.wireOp",EDGE,"E1.bottom");var subQ7=sQuery(id+"F0.wireOp",EDGE,"E1.right");var subQ8=sQuery(id+"F0.wireOp",EDGE,"E1.top");var subQ9=sQuery(id+"F0.wireOp",EDGE,"E1.left");var subQ10=sQuery(id+"F0.wireOp",EDGE,"E23.filletArc");var subQ11=sQuery(id+"F0.wireOp",EDGE,"E24.filletArc");Q0=makeQuery(id+"F2.boolean.opBoolean","SPLIT",FACE,{"disambiguationData":[TD([makeQuery(id+"F1.opExtrude","SWEPT_FACE",FACE,{"disambiguationData":[OSD([subQ6])]})])],"derivedFrom":makeQuery(id+"F1.opExtrude","CAP_FACE",FACE,{"disambiguationData":[OSD([subQ6,subQ8,subQ9,subQ7,subQ4,subQ3,subQ2,subQ1,subQ0,subQ5,subQ10,subQ11])],"isStart":true})});}
            var sketch = newSketch(context, id + "F16", { "sketchPlane" : qUnion([Q0])});
            skLineSegment(sketch, "E79.0", {"start": v(-70, 90) * mm, "end": v(70, 90) * mm});
            skArc(sketch, "E79.1", {"start": v(-70, 90) * mm, "mid": v(-77.07, 87.07) * mm, "end": v(-80, 80) * mm});
            skLineSegment(sketch, "E79.2", {"start": v(-80, -80) * mm, "end": v(-80, 80) * mm});
            skArc(sketch, "E79.3", {"start": v(-80, -80) * mm, "mid": v(-77.07, -87.07) * mm, "end": v(-70, -90) * mm});
            skLineSegment(sketch, "E79.4", {"start": v(-70, -90) * mm, "end": v(70, -90) * mm});
            skArc(sketch, "E79.5", {"start": v(70, -90) * mm, "mid": v(77.07, -87.07) * mm, "end": v(80, -80) * mm});
            skLineSegment(sketch, "E79.6", {"start": v(80, -80) * mm, "end": v(80, 80) * mm});
            skArc(sketch, "E79.7", {"start": v(80, 80) * mm, "mid": v(77.07, 87.07) * mm, "end": v(70, 90) * mm});
            skCircle(sketch, "E79.8", {"center": v(60, 67.5) * mm, "radius": 4 * mm});
            skCircle(sketch, "E79.9", {"center": v(60, -67.5) * mm, "radius": 4 * mm});
            skCircle(sketch, "E79.10", {"center": v(-60, -67.5) * mm, "radius": 4 * mm});
            skCircle(sketch, "E79.11", {"center": v(-60, 67.5) * mm, "radius": 4 * mm});
            skArc(sketch, "E79.12", {"start": v(56.15, 48.18) * mm, "mid": v(0, 67.5) * mm, "end": v(-56.15, 48.18) * mm});
            skArc(sketch, "E79.13", {"start": v(-56.15, 48.18) * mm, "mid": v(-58.99, 44.68) * mm, "end": v(-60, 40.3) * mm});
            skLineSegment(sketch, "E79.14", {"start": v(-60, 40.3) * mm, "end": v(-60, -40.3) * mm});
            skArc(sketch, "E79.15", {"start": v(-60, -40.3) * mm, "mid": v(-58.99, -44.68) * mm, "end": v(-56.15, -48.18) * mm});
            skArc(sketch, "E79.16", {"start": v(-56.15, -48.18) * mm, "mid": v(0, -67.5) * mm, "end": v(56.15, -48.18) * mm});
            skArc(sketch, "E79.17", {"start": v(56.15, -48.18) * mm, "mid": v(58.99, -44.68) * mm, "end": v(60, -40.3) * mm});
            skLineSegment(sketch, "E79.18", {"start": v(60, 40.3) * mm, "end": v(60, -40.3) * mm});
            skArc(sketch, "E79.19", {"start": v(60, 40.3) * mm, "mid": v(58.99, 44.68) * mm, "end": v(56.15, 48.18) * mm});
            skCircle(sketch, "E80", {"center": v(0, 120) * mm, "radius": 6 * mm});
            skArc(sketch, "E81", {"start": v(15, 120) * mm, "mid": v(0, 135) * mm, "end": v(-15, 120) * mm});
            skLineSegment(sketch, "E82", {"start": v(-15, 120) * mm, "end": v(-15, 108) * mm});
            skLineSegment(sketch, "E83", {"start": v(15, 120) * mm, "end": v(15, 108) * mm});
            skLineSegment(sketch, "E84", {"start": v(15, 108) * mm, "end": v(33, 90) * mm});
            skLineSegment(sketch, "E85", {"start": v(-15, 108) * mm, "end": v(-33, 90) * mm});
            skLineSegment(sketch, "E86", {"start": v(0, 120) * mm, "end": v(0, 90) * mm, "construction": true});
            skLineSegment(sketch, "E87", {"start": v(-80, 0) * mm, "end": v(80, 0) * mm, "construction": true});
            skCircle(sketch, "E88.MirrorC", {"center": v(0, -120) * mm, "radius": 6 * mm});
            skLineSegment(sketch, "E89.MirrorCS", {"start": v(0, -120) * mm, "end": v(0, -90) * mm, "construction": true});
            skLineSegment(sketch, "E90.MirrorCS", {"start": v(15, -120) * mm, "end": v(15, -108) * mm});
            skArc(sketch, "E91.MirrorCS", {"start": v(15, -120) * mm, "mid": v(0, -135) * mm, "end": v(-15, -120) * mm});
            skLineSegment(sketch, "E92.MirrorCS", {"start": v(-15, -120) * mm, "end": v(-15, -108) * mm});
            skLineSegment(sketch, "E93.MirrorCS", {"start": v(-15, -108) * mm, "end": v(-33, -90) * mm});
            skLineSegment(sketch, "E94.MirrorCS", {"start": v(15, -108) * mm, "end": v(33, -90) * mm});
            skSolve(sketch);
        }
        {
            var Q0;
            Q0 = qSketchRegion(id + "F16", true);
            var Q1;
            Q1=makeQuery(id+"F2.opExtrude","CAP_FACE",FACE,{"disambiguationData":[OSD([sQuery(id+"F0.wireOp",EDGE,"E12"),sQuery(id+"F0.wireOp",EDGE,"E13"),sQuery(id+"F0.wireOp",EDGE,"E14"),sQuery(id+"F0.wireOp",EDGE,"E15"),sQuery(id+"F0.wireOp",EDGE,"E17.filletArc"),sQuery(id+"F0.wireOp",EDGE,"E18.filletArc"),sQuery(id+"F0.wireOp",EDGE,"E19.filletArc"),sQuery(id+"F0.wireOp",EDGE,"E20.filletArc"),sQuery(id+"F0.wireOp",EDGE,"E25.0"),sQuery(id+"F0.wireOp",EDGE,"E25.1"),sQuery(id+"F0.wireOp",EDGE,"E25.2"),sQuery(id+"F0.wireOp",EDGE,"E25.3"),sQuery(id+"F0.wireOp",EDGE,"E25.4"),sQuery(id+"F0.wireOp",EDGE,"E25.5"),sQuery(id+"F0.wireOp",EDGE,"E25.6"),sQuery(id+"F0.wireOp",EDGE,"E25.7")])],"isStart":false});
            extrude(context, id + "F17", {"entities" : qUnion([Q0]), "endBound" : BoundingType.UP_TO_SURFACE, "depth" : 25 * mm, "endBoundEntityFace" : qUnion([Q1]), "offsetDistance" : 25 * mm});
        }
    });
